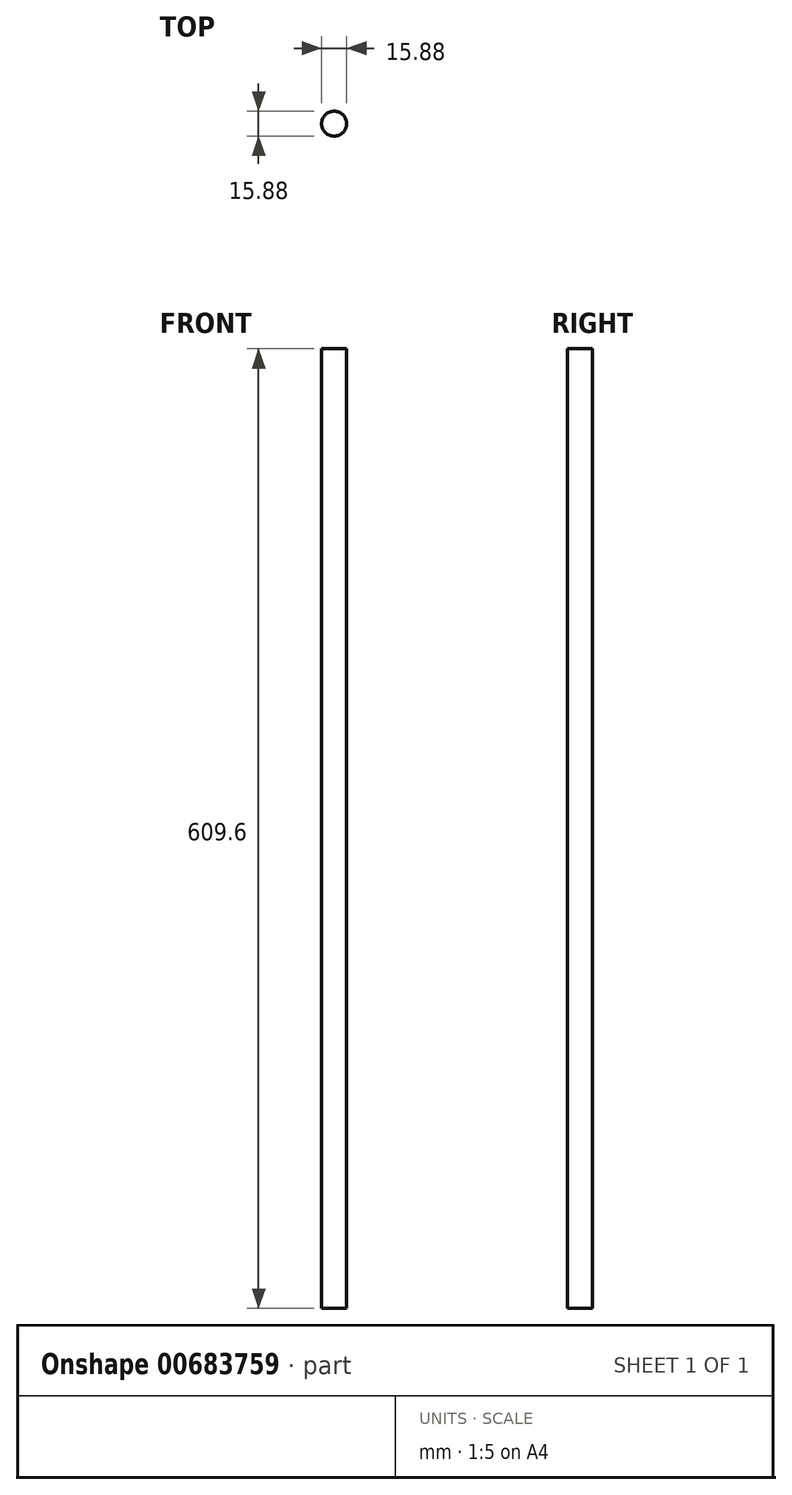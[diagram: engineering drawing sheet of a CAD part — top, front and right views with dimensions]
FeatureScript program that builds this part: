
annotation { "Feature Type Name" : "Feature", "Feature Type Description" : "" }
export const myFeature = defineFeature(function(context is Context, id is Id, definition is map)
    precondition{}
    {
        {
            var Q0;
            Q0=qCreatedBy(makeId("Top.planeOp"),FACE);
            var sketch = newSketch(context, id + "F0", { "sketchPlane" : qUnion([Q0])});
            skCircle(sketch, "E0", {"center": v(0, 0) * mm, "radius": 7.94 * mm});
            skSolve(sketch);
        }
        {
            var Q0;
            Q0 = qSketchRegion(id + "F0", true);
            extrude(context, id + "F1", {"entities" : qUnion([Q0]), "depth" : 609.6 * mm, "offsetDistance" : 25.4 * mm});
        }
    });
